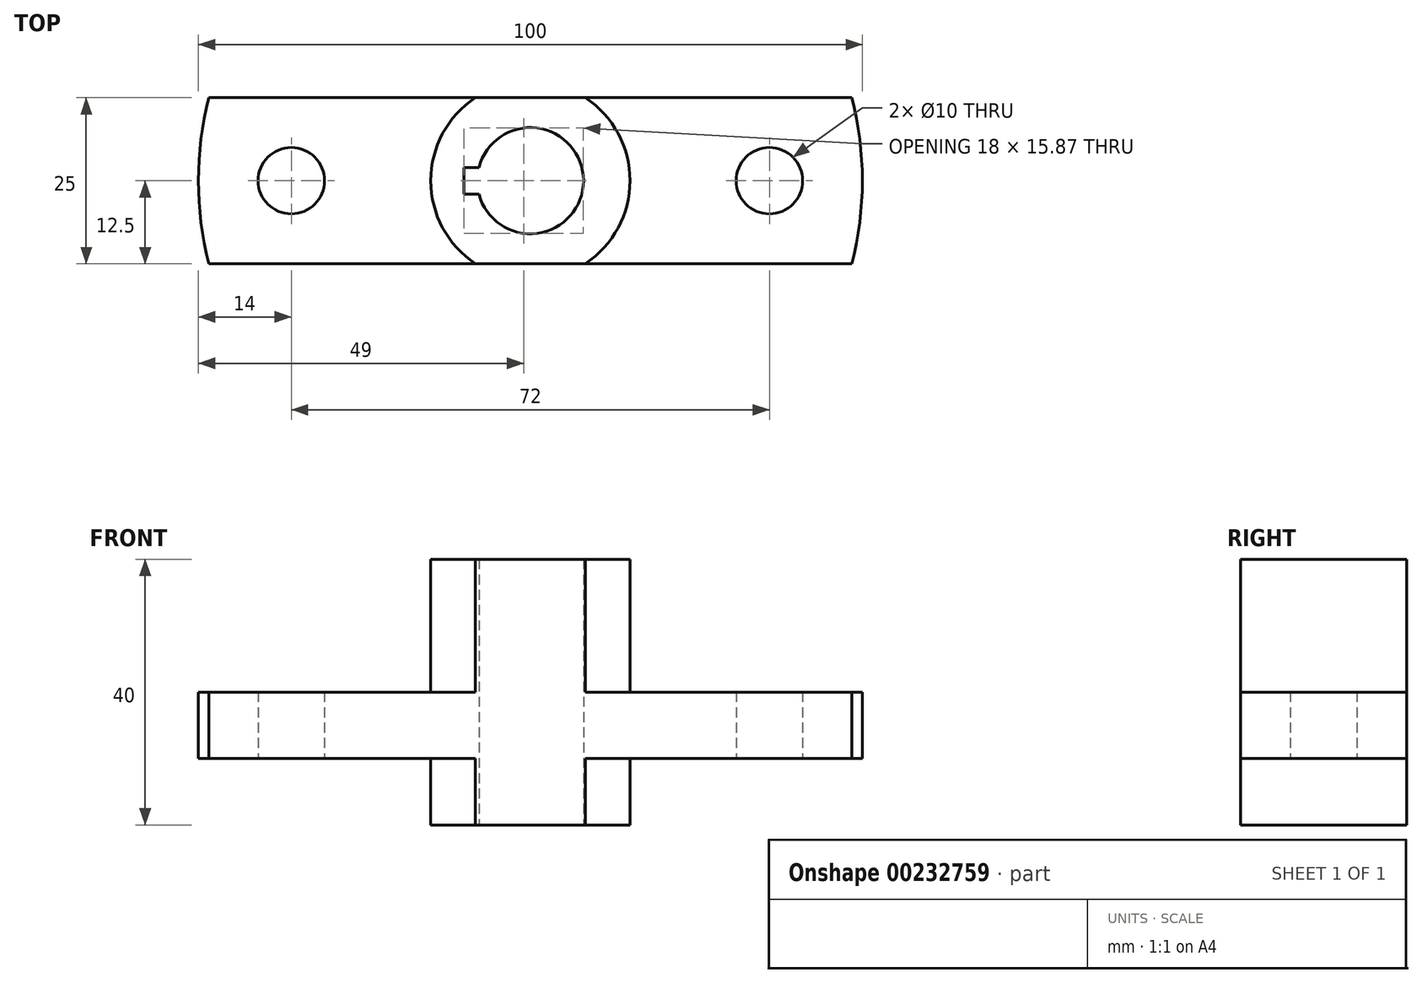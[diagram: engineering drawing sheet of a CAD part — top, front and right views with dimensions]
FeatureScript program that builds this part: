
annotation { "Feature Type Name" : "Feature", "Feature Type Description" : "" }
export const myFeature = defineFeature(function(context is Context, id is Id, definition is map)
    precondition{}
    {
        {
            var Q0;
            Q0=qCreatedBy(makeId("Top.planeOp"),FACE);
            var sketch = newSketch(context, id + "F0", { "sketchPlane" : qUnion([Q0])});
            skArc(sketch, "E0", {"start": v(-48.41, 12.5) * mm, "mid": v(-50, 0) * mm, "end": v(-48.41, -12.5) * mm});
            skArc(sketch, "E1", {"start": v(-7.75, -2) * mm, "mid": v(8, 0) * mm, "end": v(-7.75, 2) * mm});
            skArc(sketch, "E2", {"start": v(8.3, -12.5) * mm, "mid": v(15, 0) * mm, "end": v(8.3, 12.5) * mm});
            skCircle(sketch, "E3", {"center": v(-36, 0) * mm, "radius": 5 * mm});
            skCircle(sketch, "E4", {"center": v(36, 0) * mm, "radius": 5 * mm});
            skLineSegment(sketch, "E5", {"start": v(-48.41, 12.5) * mm, "end": v(48.41, 12.5) * mm});
            skLineSegment(sketch, "E6", {"start": v(-48.41, -12.5) * mm, "end": v(48.41, -12.5) * mm});
            skLineSegment(sketch, "E7", {"start": v(-7.75, 2) * mm, "end": v(-10, 2) * mm});
            skLineSegment(sketch, "E8", {"start": v(-10, 2) * mm, "end": v(-10, -2) * mm});
            skLineSegment(sketch, "E9", {"start": v(-10, -2) * mm, "end": v(-7.75, -2) * mm});
            skArc(sketch, "E10.trimOffspring", {"start": v(48.41, -12.5) * mm, "mid": v(50, 0) * mm, "end": v(48.41, 12.5) * mm});
            skArc(sketch, "E11.trimOffspring", {"start": v(-8.3, 12.5) * mm, "mid": v(-15, 0) * mm, "end": v(-8.3, -12.5) * mm});
            skSolve(sketch);
        }
        {
            var Q0;
            {var subQ1=sQuery(id+"F0.wireOp",EDGE,"E2");Q0=makeQuery(id+"F0.imprint","IMPRINT",FACE,{"disambiguationData":[TD([[makeQuery(id+"F0.imprint","IMPRINT",EDGE,{"derivedFrom":subQ1}),-1.0]])]});}
            var Q1;
            {var subQ1=sQuery(id+"F0.wireOp",EDGE,"E0");Q1=makeQuery(id+"F0.imprint","IMPRINT",FACE,{"disambiguationData":[TD([[makeQuery(id+"F0.imprint","IMPRINT",EDGE,{"derivedFrom":subQ1}),1.0]])]});}
            var Q2;
            Q2 = qSketchRegion(id + "F2", true);
            var Q3;
            Q3=makeQuery(id+"F0.imprint","IMPRINT",FACE,{"disambiguationData":[TD([[makeQuery(id+"F0.imprint","IMPRINT",EDGE,{"derivedFrom":sQuery(id+"F0.wireOp",EDGE,"E1")}),-1.0]])]});
            extrude(context, id + "F1", {"entities" : qUnion([Q0, Q1, Q2, Q3]), "depth" : 10 * mm});
        }
        {
            var Q0;
            Q0=makeQuery(id+"F1.opExtrude","SWEPT_FACE",FACE,{"disambiguationData":[OSD([sQuery(id+"F0.wireOp",EDGE,"E6")])]});
            var sketch = newSketch(context, id + "F2", { "sketchPlane" : qUnion([Q0])});
            skSolve(sketch);
        }
        {
            var Q0;
            Q0=makeQuery(id+"F0.imprint","IMPRINT",FACE,{"disambiguationData":[TD([[makeQuery(id+"F0.imprint","IMPRINT",EDGE,{"derivedFrom":sQuery(id+"F0.wireOp",EDGE,"E1")}),-1.0]])]});
            extrude(context, id + "F3", {"entities" : qUnion([Q0]), "operationType" : NewBodyOperationType.ADD, "depth" : 30 * mm});
        }
        {
            var Q0;
            Q0=makeQuery(id+"F0.imprint","IMPRINT",FACE,{"disambiguationData":[TD([[makeQuery(id+"F0.imprint","IMPRINT",EDGE,{"derivedFrom":sQuery(id+"F0.wireOp",EDGE,"E1")}),-1.0]])]});
            extrude(context, id + "F4", {"entities" : qUnion([Q0]), "operationType" : NewBodyOperationType.ADD, "oppositeDirection" : true, "depth" : 10 * mm});
        }
    });
